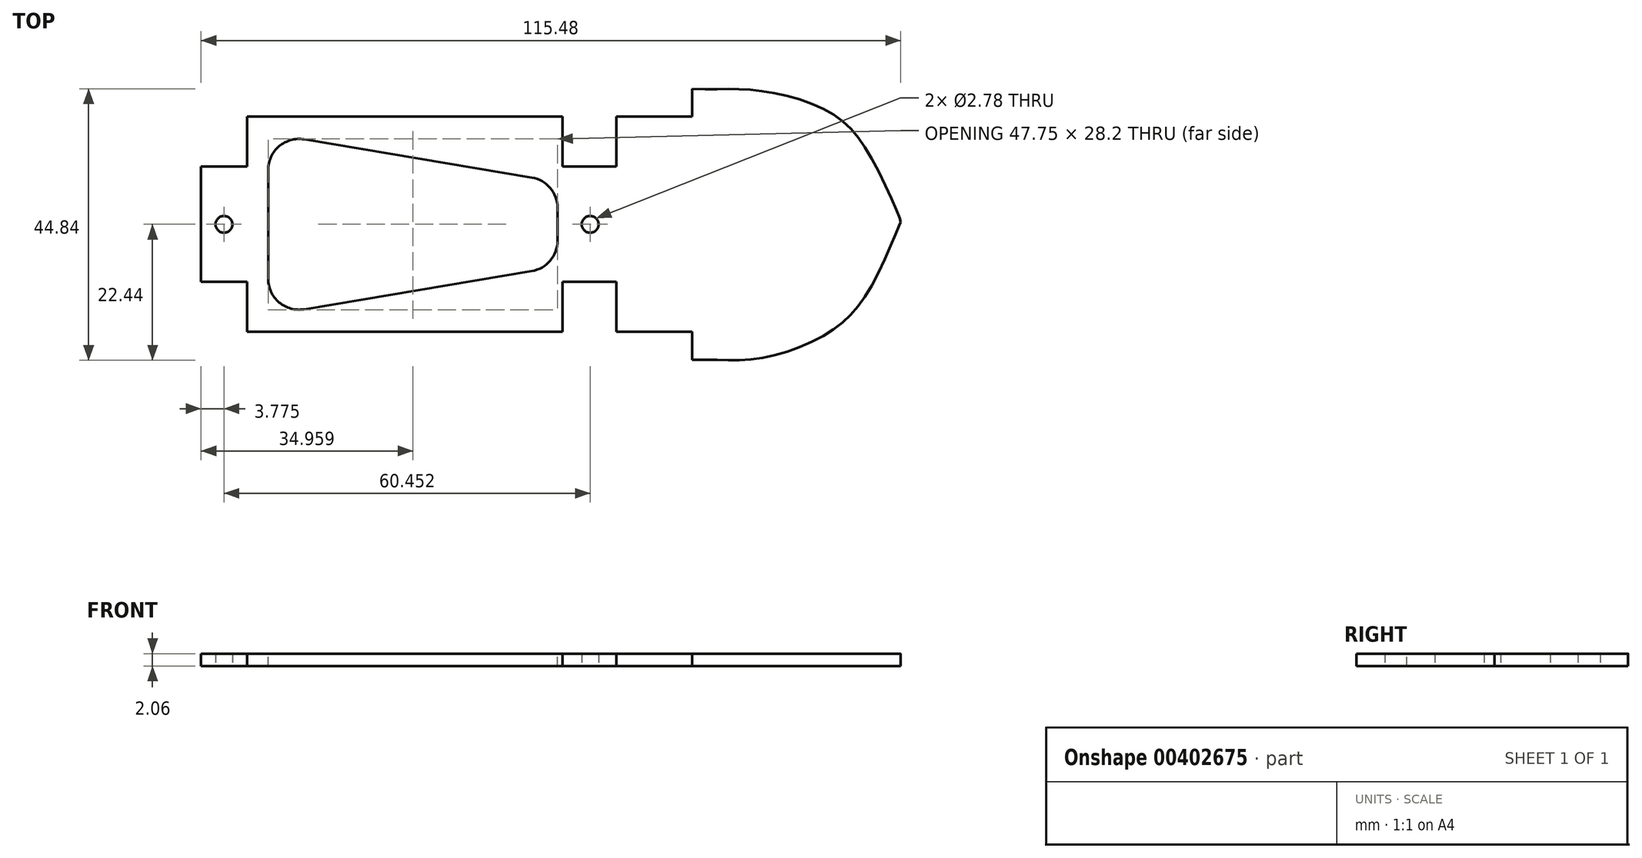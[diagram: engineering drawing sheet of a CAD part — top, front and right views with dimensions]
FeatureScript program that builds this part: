
annotation { "Feature Type Name" : "Feature", "Feature Type Description" : "" }
export const myFeature = defineFeature(function(context is Context, id is Id, definition is map)
    precondition{}
    {
        {
            var Q0;
            Q0=qCreatedBy(makeId("Top.planeOp"),FACE);
            var sketch = newSketch(context, id + "F0", { "sketchPlane" : qUnion([Q0])});
            skLineSegment(sketch, "E0.bottom", {"start": v(50.8, -9.52) * mm, "end": v(-50.8, -9.53) * mm});
            skLineSegment(sketch, "E0.top", {"start": v(50.8, 9.53) * mm, "end": v(-50.8, 9.52) * mm});
            skLineSegment(sketch, "E0.left", {"start": v(50.8, -9.52) * mm, "end": v(50.8, 9.53) * mm});
            skLineSegment(sketch, "E0.right", {"start": v(-50.8, -9.53) * mm, "end": v(-50.8, 9.52) * mm});
            skPoint(sketch, "E0.middle", {"position": v(0, 0) * mm});
            skLineSegment(sketch, "E1.bottom", {"start": v(-43.18, 17.78) * mm, "end": v(8.89, 17.78) * mm});
            skLineSegment(sketch, "E1.top", {"start": v(-43.18, -17.78) * mm, "end": v(8.89, -17.78) * mm});
            skLineSegment(sketch, "E1.left", {"start": v(-43.18, 17.78) * mm, "end": v(-43.18, -17.78) * mm});
            skLineSegment(sketch, "E1.right", {"start": v(8.89, 17.78) * mm, "end": v(8.89, -17.78) * mm});
            skPoint(sketch, "E1.middle", {"position": v(-17.15, 0) * mm});
            skCircle(sketch, "E2", {"center": v(-47.03, 0) * mm, "radius": 1.39 * mm});
            skPoint(sketch, "E2.centerSnap0", {"position": v(-43.18, 0) * mm});
            skCircle(sketch, "E3", {"center": v(13.43, 0) * mm, "radius": 1.39 * mm});
            skSolve(sketch);
        }
        {
            var Q0;
            Q0=qSketchRegion(id+"F0",true);
            extrude(context, id + "F1", {"entities" : qUnion([Q0]), "depth" : 2.06 * mm, "offsetDistance" : 25.4 * mm});
        }
        {
            var Q0;
            Q0=qCreatedBy(makeId("Top.planeOp"),FACE);
            var sketch = newSketch(context, id + "F2", { "sketchPlane" : qUnion([Q0])});
            skFitSpline(sketch, "E4", {"points": [v(30.28, 22.4) * mm, v(41.02, 22.12) * mm, v(53.24, 18.36) * mm, v(60.42, 9.9) * mm, v(64.67, 0.37) * mm, v(64.55, 0.37) * mm], "startDerivative": vector(52.83, -2) * mm, "endDerivative": vector(-5.96, 2.28) * mm});
            skFitSpline(sketch, "E5.MirrorCS", {"points": [v(30.28, -22.4) * mm, v(41.13, -22.18) * mm, v(53.24, -17.61) * mm, v(60.42, -9.15) * mm, v(64.67, 0.37) * mm, v(64.55, 0.37) * mm], "startDerivative": vector(52.83, 2) * mm, "endDerivative": vector(-13.98, 0) * mm});
            skLineSegment(sketch, "E6", {"start": v(17.78, 0) * mm, "end": v(17.78, -17.78) * mm});
            skLineSegment(sketch, "E7", {"start": v(17.78, -17.78) * mm, "end": v(30.28, -17.78) * mm});
            skLineSegment(sketch, "E8", {"start": v(30.28, -17.78) * mm, "end": v(30.28, -22.4) * mm});
            skLineSegment(sketch, "E9.MirrorCS", {"start": v(17.78, 0) * mm, "end": v(17.78, 17.78) * mm});
            skLineSegment(sketch, "E10.MirrorCS", {"start": v(17.78, 17.78) * mm, "end": v(30.28, 17.78) * mm});
            skLineSegment(sketch, "E11.MirrorCS", {"start": v(30.28, 17.78) * mm, "end": v(30.28, 22.4) * mm});
            skSolve(sketch);
        }
        {
            var Q0;
            Q0=qSketchRegion(id+"F2",true);
            extrude(context, id + "F3", {"entities" : qUnion([Q0]), "operationType" : NewBodyOperationType.ADD, "depth" : 2.06 * mm, "offsetDistance" : 25.4 * mm});
        }
        {
            var Q0;
            Q0=qCreatedBy(makeId("Top.planeOp"),FACE);
            var sketch = newSketch(context, id + "F4", { "sketchPlane" : qUnion([Q0])});
            skLineSegment(sketch, "E12", {"start": v(8.04, 0) * mm, "end": v(8.04, 7.01) * mm});
            skLineSegment(sketch, "E13", {"start": v(8.04, 7.01) * mm, "end": v(-39.72, 15.03) * mm});
            skLineSegment(sketch, "E14", {"start": v(-39.72, 15.03) * mm, "end": v(-39.72, 0) * mm});
            skLineSegment(sketch, "E15.MirrorCS", {"start": v(-39.72, -15.03) * mm, "end": v(-39.72, 0) * mm});
            skLineSegment(sketch, "E16.MirrorCS", {"start": v(8.04, -7.01) * mm, "end": v(-39.72, -15.03) * mm});
            skLineSegment(sketch, "E17.MirrorCS", {"start": v(8.04, 0) * mm, "end": v(8.04, -7.01) * mm});
            skSolve(sketch);
        }
        {
            var Q0;
            Q0 = qSketchRegion(id + "F4", true);
            extrude(context, id + "F5", {"entities" : qUnion([Q0]), "operationType" : NewBodyOperationType.REMOVE, "endBound" : BoundingType.SYMMETRIC, "oppositeDirection" : true, "depth" : 25.4 * mm, "offsetDistance" : 25.4 * mm});
        }
        {
            var Q0;
            Q0=makeQuery(id+"F5.boolean.opBoolean","COPY",EDGE,{"derivedFrom":makeQuery(id+"F5.opExtrude","SWEPT_EDGE",EDGE,{"disambiguationData":[OSD([sQuery(id+"F4.wireOp",EDGE,"E13"),sQuery(id+"F4.wireOp",EDGE,"E14")])]})});
            var Q1;
            Q1=makeQuery(id+"F5.boolean.opBoolean","COPY",EDGE,{"derivedFrom":makeQuery(id+"F5.opExtrude","SWEPT_EDGE",EDGE,{"disambiguationData":[OSD([sQuery(id+"F4.wireOp",EDGE,"E12"),sQuery(id+"F4.wireOp",EDGE,"E13")])]})});
            var Q2;
            Q2=makeQuery(id+"F5.boolean.opBoolean","COPY",EDGE,{"derivedFrom":makeQuery(id+"F5.opExtrude","SWEPT_EDGE",EDGE,{"disambiguationData":[OSD([sQuery(id+"F4.wireOp",EDGE,"E16.MirrorCS"),sQuery(id+"F4.wireOp",EDGE,"E17.MirrorCS")])]})});
            var Q3;
            Q3=makeQuery(id+"F5.boolean.opBoolean","COPY",EDGE,{"derivedFrom":makeQuery(id+"F5.opExtrude","SWEPT_EDGE",EDGE,{"disambiguationData":[OSD([sQuery(id+"F4.wireOp",EDGE,"E15.MirrorCS"),sQuery(id+"F4.wireOp",EDGE,"E16.MirrorCS")])]})});
            fillet(context, id + "F6", {"entities" : qUnion([Q0, Q1, Q2, Q3]), "radius" : 5.08 * mm, "tangentPropagation" : true, "allowEdgeOverflow" : false});
        }
    });
